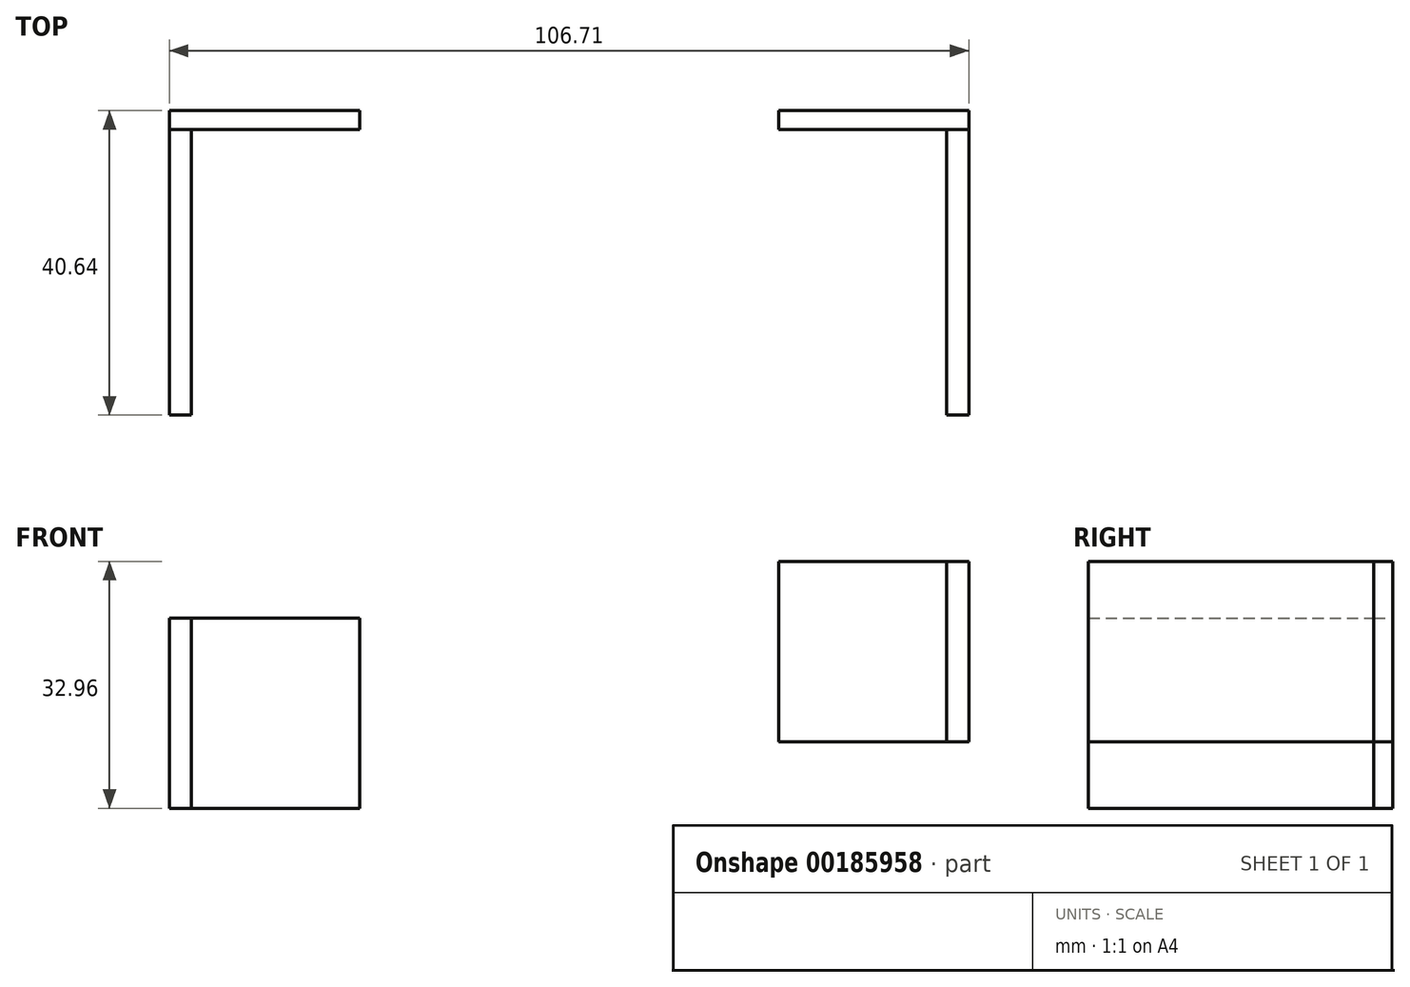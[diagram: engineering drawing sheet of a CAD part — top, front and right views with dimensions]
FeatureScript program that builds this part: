
annotation { "Feature Type Name" : "Feature", "Feature Type Description" : "" }
export const myFeature = defineFeature(function(context is Context, id is Id, definition is map)
    precondition{}
    {
        {
            var Q0;
            Q0=qCreatedBy(makeId("Front.planeOp"),FACE);
            var sketch = newSketch(context, id + "F0", { "sketchPlane" : qUnion([Q0])});
            skLineSegment(sketch, "E0.bottom", {"start": v(-68.74, -44.28) * mm, "end": v(-43.34, -44.28) * mm});
            skLineSegment(sketch, "E0.top", {"start": v(-68.74, -18.88) * mm, "end": v(-43.34, -18.88) * mm});
            skLineSegment(sketch, "E0.left", {"start": v(-68.74, -44.28) * mm, "end": v(-68.74, -18.88) * mm});
            skLineSegment(sketch, "E0.right", {"start": v(-43.34, -44.28) * mm, "end": v(-43.34, -18.88) * mm});
            skLineSegment(sketch, "E1.bottom", {"start": v(12.57, -35.44) * mm, "end": v(37.97, -35.44) * mm});
            skLineSegment(sketch, "E1.top", {"start": v(12.57, -11.32) * mm, "end": v(37.97, -11.32) * mm});
            skLineSegment(sketch, "E1.left", {"start": v(12.57, -35.44) * mm, "end": v(12.57, -11.32) * mm});
            skLineSegment(sketch, "E1.right", {"start": v(37.97, -35.44) * mm, "end": v(37.97, -11.32) * mm});
            skSolve(sketch);
        }
        {
            var Q0;
            Q0=makeQuery(id+"F0.imprint","IMPRINT",FACE,{"disambiguationData":[TD([[makeQuery(id+"F0.imprint","IMPRINT",EDGE,{"derivedFrom":sQuery(id+"F0.wireOp",EDGE,"E1.bottom")}),1.0]])]});
            var Q1;
            Q1=makeQuery(id+"F0.imprint","IMPRINT",FACE,{"disambiguationData":[TD([[makeQuery(id+"F0.imprint","IMPRINT",EDGE,{"derivedFrom":sQuery(id+"F0.wireOp",EDGE,"E0.bottom")}),1.0]])]});
            extrude(context, id + "F1", {"entities" : qUnion([Q0, Q1]), "depth" : 2.54 * mm});
        }
        {
            var Q0;
            Q0=makeQuery(id+"F1.opExtrude","CAP_FACE",FACE,{"disambiguationData":[OSD([sQuery(id+"F0.wireOp",EDGE,"E0.bottom"),sQuery(id+"F0.wireOp",EDGE,"E0.top"),sQuery(id+"F0.wireOp",EDGE,"E0.left"),sQuery(id+"F0.wireOp",EDGE,"E0.right")])],"isStart":false});
            var sketch = newSketch(context, id + "F2", { "sketchPlane" : qUnion([Q0])});
            skLineSegment(sketch, "E2.bottom", {"start": v(-68.74, -18.88) * mm, "end": v(-65.8, -18.88) * mm});
            skLineSegment(sketch, "E2.top", {"start": v(-68.74, -44.28) * mm, "end": v(-65.8, -44.28) * mm});
            skLineSegment(sketch, "E2.left", {"start": v(-68.74, -18.88) * mm, "end": v(-68.74, -44.28) * mm});
            skLineSegment(sketch, "E2.right", {"start": v(-65.8, -18.88) * mm, "end": v(-65.8, -44.28) * mm});
            skSolve(sketch);
        }
        {
            var Q0;
            Q0=makeQuery(id+"F1.opExtrude","CAP_FACE",FACE,{"disambiguationData":[OSD([sQuery(id+"F0.wireOp",EDGE,"E1.bottom"),sQuery(id+"F0.wireOp",EDGE,"E1.top"),sQuery(id+"F0.wireOp",EDGE,"E1.left"),sQuery(id+"F0.wireOp",EDGE,"E1.right")])],"isStart":false});
            var sketch = newSketch(context, id + "F3", { "sketchPlane" : qUnion([Q0])});
            skLineSegment(sketch, "E3.bottom", {"start": v(37.97, -11.32) * mm, "end": v(35.04, -11.32) * mm});
            skLineSegment(sketch, "E3.top", {"start": v(37.97, -35.44) * mm, "end": v(35.04, -35.44) * mm});
            skLineSegment(sketch, "E3.left", {"start": v(37.97, -11.32) * mm, "end": v(37.97, -35.44) * mm});
            skLineSegment(sketch, "E3.right", {"start": v(35.04, -11.32) * mm, "end": v(35.04, -35.44) * mm});
            skSolve(sketch);
        }
        {
            var Q0;
            Q0=makeQuery(id+"F2.imprint","IMPRINT",FACE,{"disambiguationData":[TD([[makeQuery(id+"F2.imprint","IMPRINT",EDGE,{"derivedFrom":sQuery(id+"F2.wireOp",EDGE,"E2.bottom")}),-1.0]])]});
            var Q1;
            Q1=makeQuery(id+"F3.imprint","IMPRINT",FACE,{"disambiguationData":[TD([[makeQuery(id+"F3.imprint","IMPRINT",EDGE,{"derivedFrom":sQuery(id+"F3.wireOp",EDGE,"E3.bottom")}),-1.0]])]});
            extrude(context, id + "F4", {"entities" : qUnion([Q0, Q1]), "depth" : 38.1 * mm});
        }
    });
